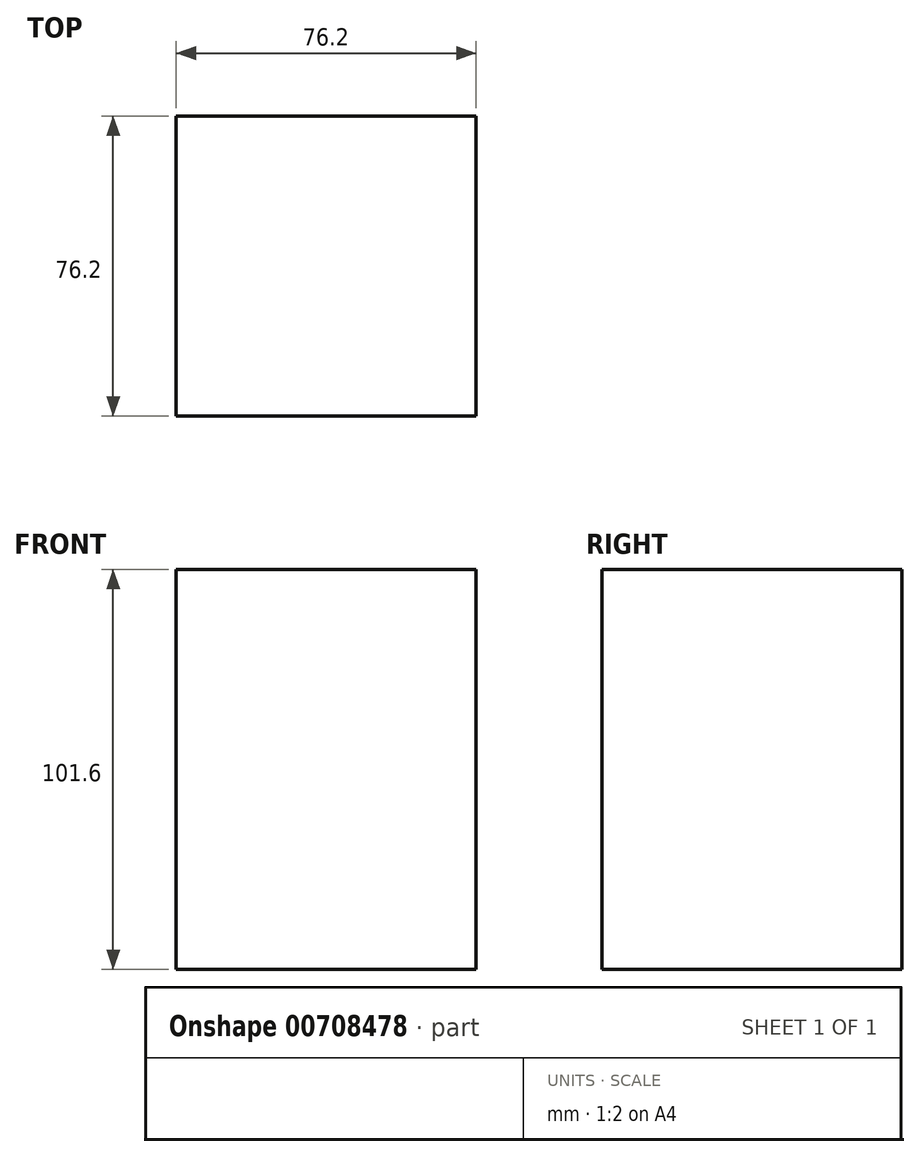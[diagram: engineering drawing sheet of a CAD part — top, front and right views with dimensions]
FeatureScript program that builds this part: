
annotation { "Feature Type Name" : "Feature", "Feature Type Description" : "" }
export const myFeature = defineFeature(function(context is Context, id is Id, definition is map)
    precondition{}
    {
        {
            var Q0;
            Q0=qCreatedBy(makeId("Front.planeOp"),FACE);
            var sketch = newSketch(context, id + "F0", { "sketchPlane" : qUnion([Q0])});
            skLineSegment(sketch, "E0.bottom", {"start": v(-38.1, -50.8) * mm, "end": v(38.1, -50.8) * mm});
            skLineSegment(sketch, "E0.top", {"start": v(-38.1, 50.8) * mm, "end": v(38.1, 50.8) * mm});
            skLineSegment(sketch, "E0.left", {"start": v(-38.1, -50.8) * mm, "end": v(-38.1, 50.8) * mm});
            skLineSegment(sketch, "E0.right", {"start": v(38.1, -50.8) * mm, "end": v(38.1, 50.8) * mm});
            skPoint(sketch, "E0.middle", {"position": v(0, 0) * mm});
            skSolve(sketch);
        }
        {
            var Q0;
            Q0 = qSketchRegion(id + "F0", true);
            extrude(context, id + "F1", {"entities" : qUnion([Q0]), "depth" : 76.2 * mm, "offsetDistance" : 25.4 * mm});
        }
    });
